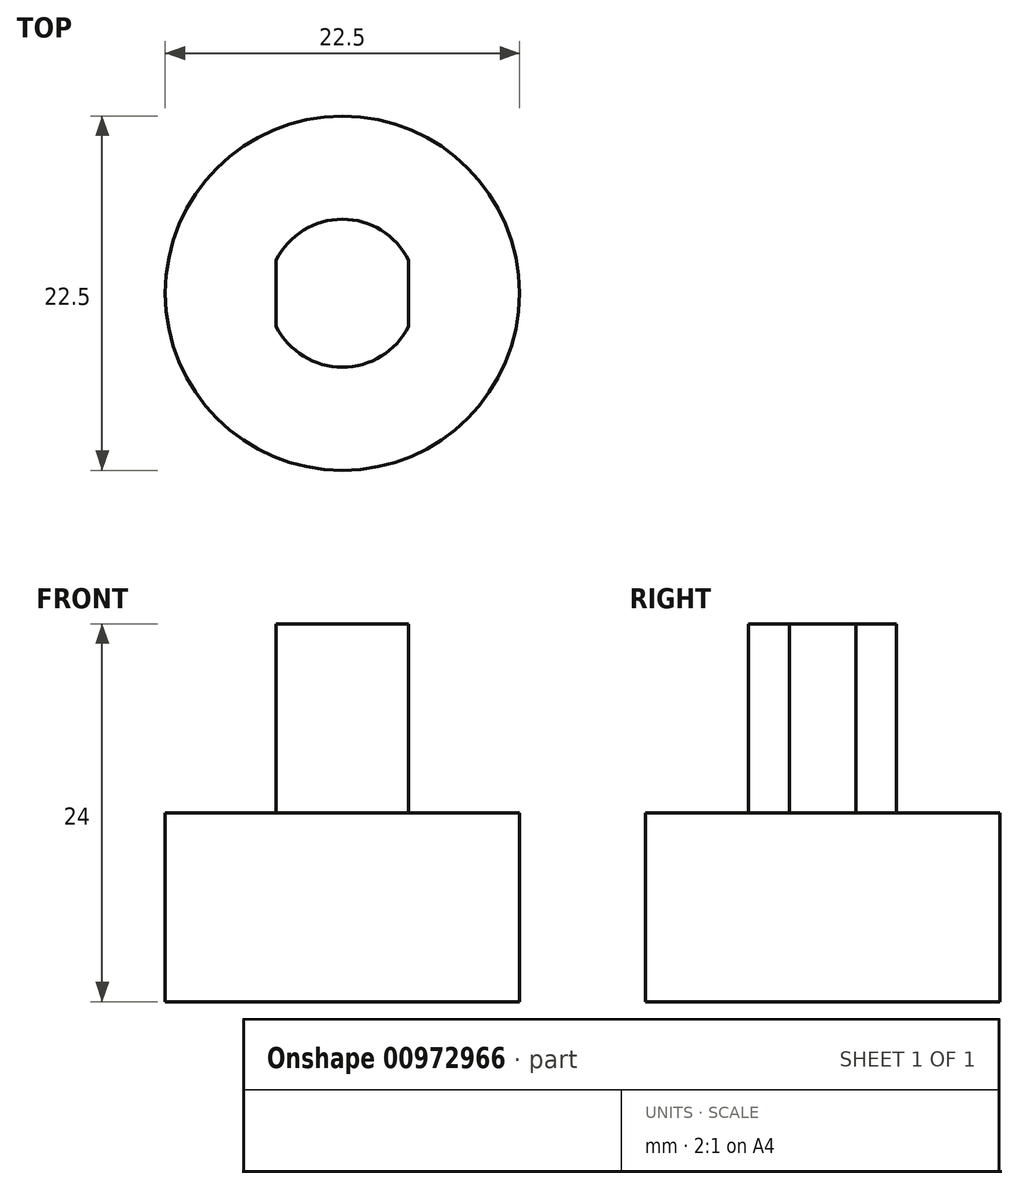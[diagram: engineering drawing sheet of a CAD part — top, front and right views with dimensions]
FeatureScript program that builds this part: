
annotation { "Feature Type Name" : "Feature", "Feature Type Description" : "" }
export const myFeature = defineFeature(function(context is Context, id is Id, definition is map)
    precondition{}
    {
        {
            var Q0;
            Q0=qCreatedBy(makeId("Top.planeOp"),FACE);
            var sketch = newSketch(context, id + "F0", { "sketchPlane" : qUnion([Q0])});
            skCircle(sketch, "E0", {"center": v(0, 0) * mm, "radius": 11.25 * mm});
            skSolve(sketch);
        }
        {
            var Q0;
            Q0 = qSketchRegion(id + "F0", true);
            extrude(context, id + "F1", {"entities" : qUnion([Q0]), "depth" : 12 * mm, "offsetDistance" : 25 * mm});
        }
        {
            var Q0;
            Q0=makeQuery(id+"F1.opExtrude","CAP_FACE",FACE,{"disambiguationData":[OSD([sQuery(id+"F0.wireOp",EDGE,"E0")])],"isStart":false});
            var sketch = newSketch(context, id + "F2", { "sketchPlane" : qUnion([Q0])});
            skArc(sketch, "E1", {"start": v(4.2, 2.1) * mm, "mid": v(0, 4.7) * mm, "end": v(-4.2, 2.1) * mm});
            skLineSegment(sketch, "E2.left", {"start": v(4.2, -2.1) * mm, "end": v(4.2, 2.1) * mm});
            skLineSegment(sketch, "E2.right", {"start": v(-4.2, -2.1) * mm, "end": v(-4.2, 2.1) * mm});
            skArc(sketch, "E3.trimOffspring", {"start": v(-4.2, -2.1) * mm, "mid": v(0, -4.7) * mm, "end": v(4.2, -2.1) * mm});
            skSolve(sketch);
        }
        {
            var Q0;
            Q0 = qSketchRegion(id + "F2", true);
            extrude(context, id + "F3", {"entities" : qUnion([Q0]), "operationType" : NewBodyOperationType.ADD, "depth" : 12 * mm, "offsetDistance" : 25 * mm});
        }
    });
